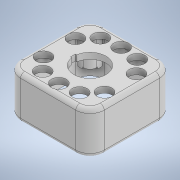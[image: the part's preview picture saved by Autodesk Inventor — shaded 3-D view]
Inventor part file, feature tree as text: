
AUTODESK INVENTOR PART (.ipt)
format: ipt  version: 2020 (Build 240168000, 168)  size: 769,536 bytes
history: native  units: mm
features: other x6, extrude x4, sketch x4, fillet x3
ambient origin geometry x8: Origin, YZ Plane, XZ Plane, XY Plane, X Axis, Y Axis, Z Axis, Center Point
bodies: Solid1 (feature_tree)
feature tree (17):
  other  "camera-back.ipt"
  extrude  "Extrusion1"  Depth=2.0mm
  extrude  "Extrusion5"  Depth=2.0mm TaperAngle=0.0deg
  extrude  "Extrusion6"  Depth=7.3mm
  extrude  "Extrusion7"  Depth=2.0mm
  fillet  "Fillet7"  Radius=7.3mm
  fillet  "Fillet8"  Radius=7.3mm
  fillet  "Fillet9"  Radius=7.3mm
  other  "TaggingFeature1"
  other  "Srf2"
  sketch  "Sketch1"  dims[d0=10.0mm d1=2.0mm]
  sketch  "Sketch5"  dims[d2=2.0mm d3=18.0mm d4=0.0mm]
  sketch  "Sketch7"  dims[d24=5.8mm d25=7.3mm]
  sketch  "Sketch8"  dims[d26=7.3mm d27=7.3mm d28=7.3mm d29=7.3mm d30=7.3mm d31=7.3mm d32=7.3mm d33=7.3mm d34=7.3mm d35=15.3mm d36=15.8mm d37=3.0mm d38=0.0mm d41=1.1mm d42=2.35mm d43=41.2mm d44=20.6mm d45=6.0mm d46=6.0mm d47=6.0mm d48=6.0mm d49=10.0mm d50=0.0mm d51=0.25mm d52=0.25mm d53=0.25mm d54=0.25mm d55=10.0mm d56=0.0mm d57=7.0mm d58=3.0mm d59=2.0mm]
  other  "Solid1::camera-back.ipt"
  other  "Srf1"
  other  "Srf1::Derived"
